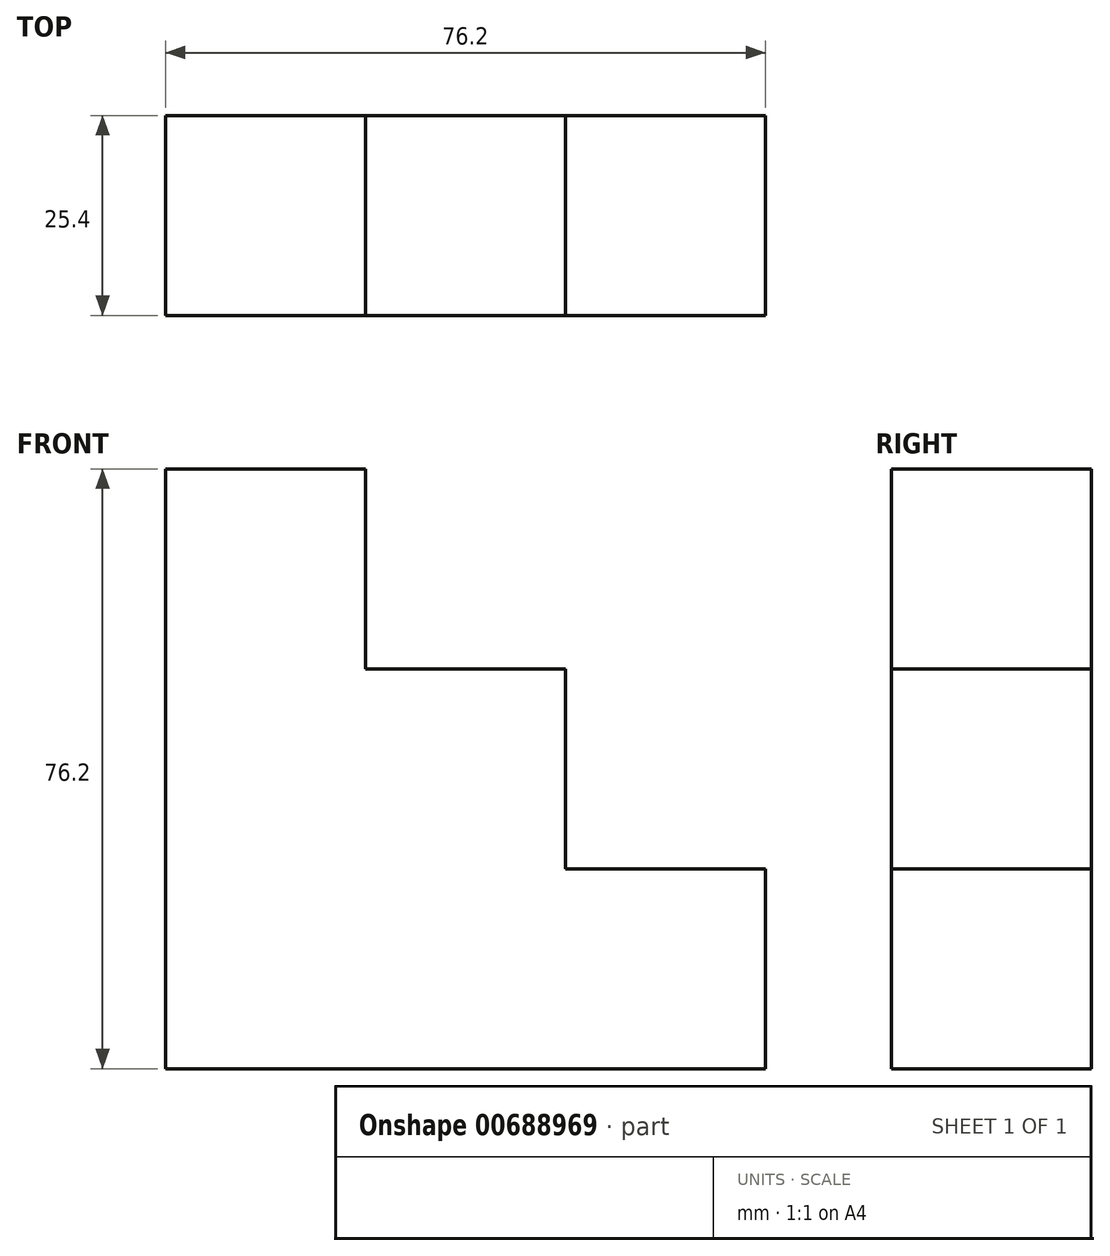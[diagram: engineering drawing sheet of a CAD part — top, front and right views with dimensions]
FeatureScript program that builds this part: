
annotation { "Feature Type Name" : "Feature", "Feature Type Description" : "" }
export const myFeature = defineFeature(function(context is Context, id is Id, definition is map)
    precondition{}
    {
        {
            var Q0;
            Q0=qCreatedBy(makeId("Front.planeOp"),FACE);
            var sketch = newSketch(context, id + "F0", { "sketchPlane" : qUnion([Q0])});
            skLineSegment(sketch, "E0", {"start": v(-28.93, 54.53) * mm, "end": v(-28.93, -21.67) * mm});
            skLineSegment(sketch, "E1", {"start": v(-28.93, -21.67) * mm, "end": v(47.27, -21.67) * mm});
            skLineSegment(sketch, "E2", {"start": v(47.27, -21.67) * mm, "end": v(47.27, 3.73) * mm});
            skLineSegment(sketch, "E3", {"start": v(47.27, 3.73) * mm, "end": v(21.87, 3.73) * mm});
            skLineSegment(sketch, "E4", {"start": v(21.87, 3.73) * mm, "end": v(21.87, 29.13) * mm});
            skLineSegment(sketch, "E5", {"start": v(21.87, 29.13) * mm, "end": v(-3.53, 29.13) * mm});
            skLineSegment(sketch, "E6", {"start": v(-3.53, 29.13) * mm, "end": v(-3.53, 54.53) * mm});
            skLineSegment(sketch, "E7", {"start": v(-3.53, 54.53) * mm, "end": v(-28.93, 54.53) * mm});
            skSolve(sketch);
        }
        {
            var Q0;
            Q0 = qSketchRegion(id + "F0", true);
            extrude(context, id + "F1", {"entities" : qUnion([Q0]), "depth" : 25.4 * mm, "offsetDistance" : 25.4 * mm});
        }
    });
